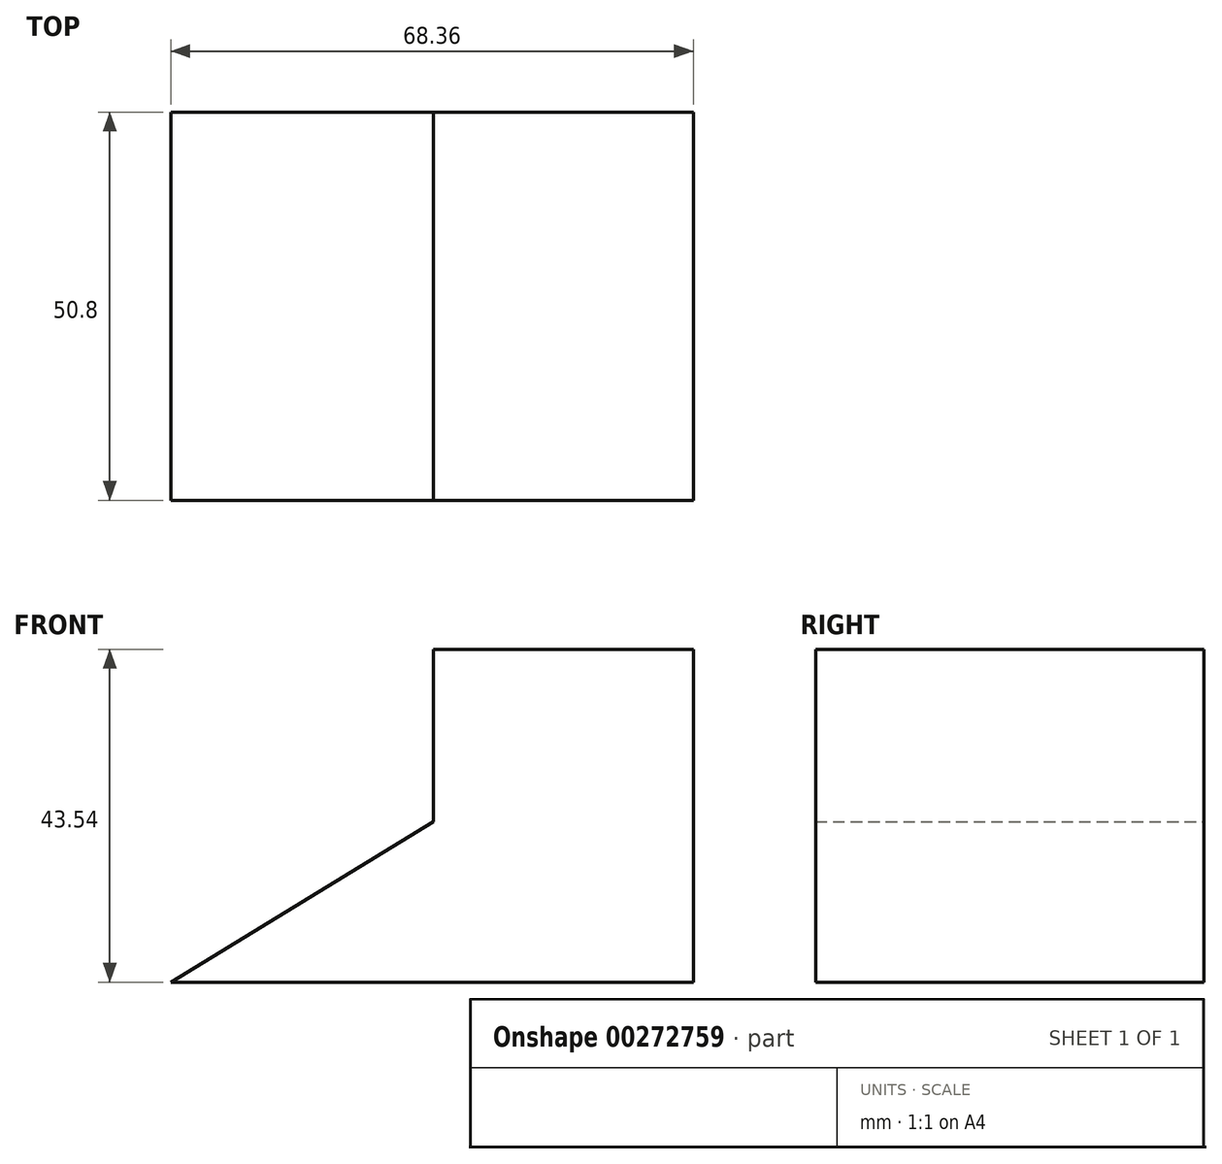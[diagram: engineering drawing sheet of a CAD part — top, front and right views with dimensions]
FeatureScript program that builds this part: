
annotation { "Feature Type Name" : "Feature", "Feature Type Description" : "" }
export const myFeature = defineFeature(function(context is Context, id is Id, definition is map)
    precondition{}
    {
        {
            var Q0;
            Q0=qCreatedBy(makeId("Front.planeOp"),FACE);
            var sketch = newSketch(context, id + "F0", { "sketchPlane" : qUnion([Q0])});
            skLineSegment(sketch, "E0", {"start": v(0, 0) * mm, "end": v(-68.36, 0) * mm});
            skLineSegment(sketch, "E1", {"start": v(-68.36, 0) * mm, "end": v(-33.99, 21) * mm});
            skLineSegment(sketch, "E2", {"start": v(-33.99, 21) * mm, "end": v(-33.99, 43.54) * mm});
            skLineSegment(sketch, "E3", {"start": v(-33.99, 43.54) * mm, "end": v(0, 43.54) * mm});
            skLineSegment(sketch, "E4", {"start": v(0, 0) * mm, "end": v(0, 43.54) * mm});
            skSolve(sketch);
        }
        {
            var Q0;
            Q0 = qSketchRegion(id + "F0", true);
            extrude(context, id + "F1", {"entities" : qUnion([Q0]), "depth" : 50.8 * mm});
        }
    });
